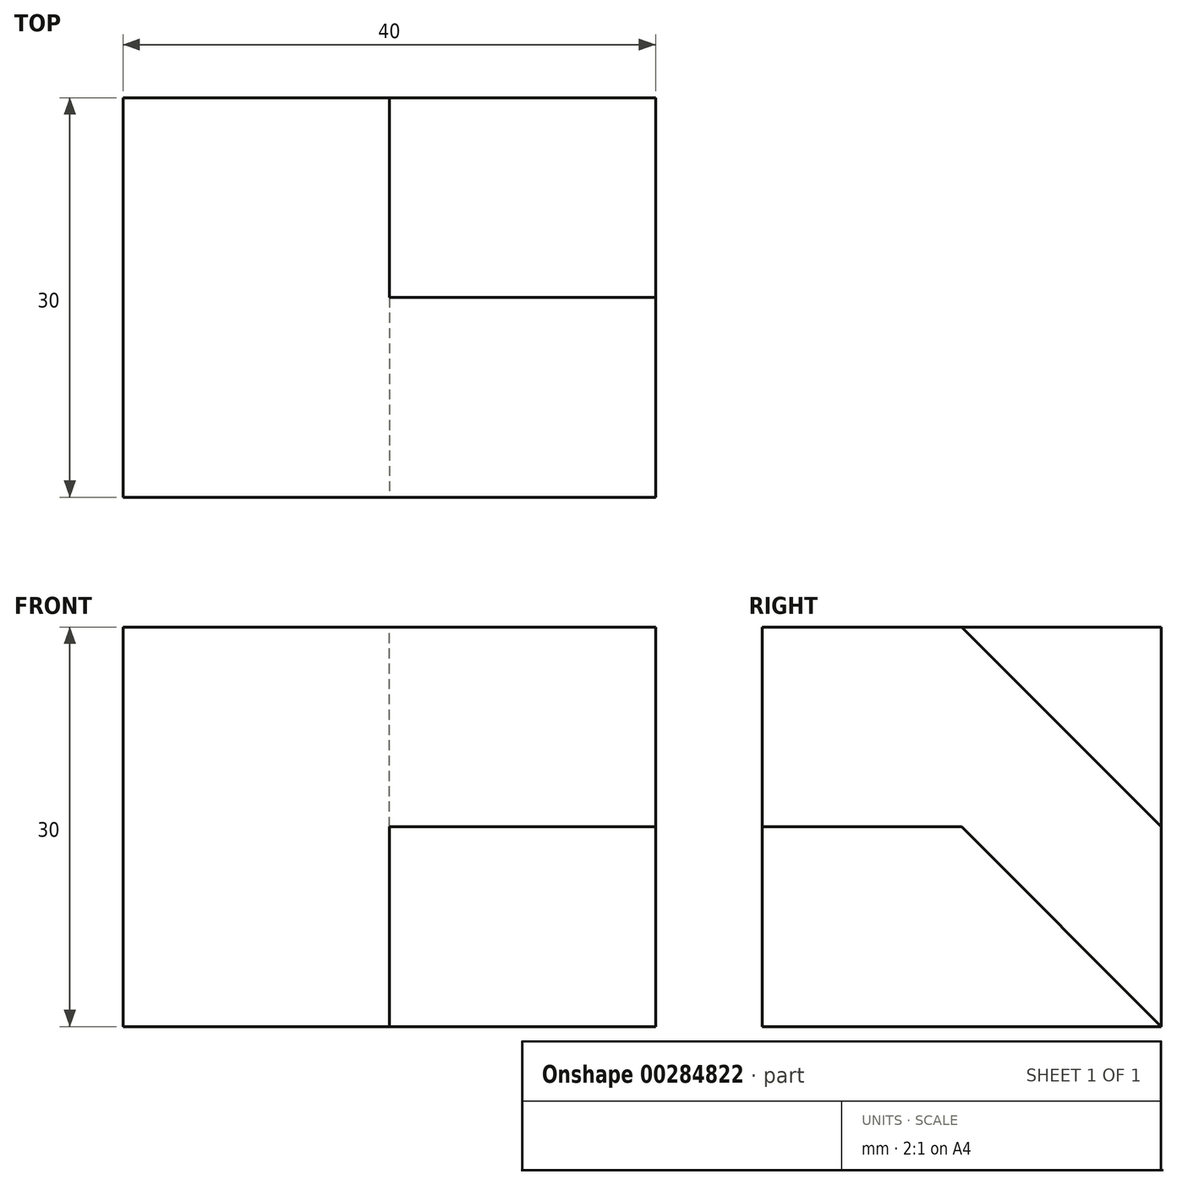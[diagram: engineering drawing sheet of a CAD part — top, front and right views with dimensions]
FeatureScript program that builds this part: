
annotation { "Feature Type Name" : "Feature", "Feature Type Description" : "" }
export const myFeature = defineFeature(function(context is Context, id is Id, definition is map)
    precondition{}
    {
        {
            var Q0;
            Q0=qCreatedBy(makeId("Right.planeOp"),FACE);
            var sketch = newSketch(context, id + "F0", { "sketchPlane" : qUnion([Q0])});
            skLineSegment(sketch, "E0.bottom", {"start": v(0, 0) * mm, "end": v(30, 0) * mm});
            skLineSegment(sketch, "E0.top", {"start": v(0, 30) * mm, "end": v(30, 30) * mm});
            skLineSegment(sketch, "E0.left", {"start": v(0, 0) * mm, "end": v(0, 30) * mm});
            skLineSegment(sketch, "E0.right", {"start": v(30, 0) * mm, "end": v(30, 30) * mm});
            skLineSegment(sketch, "E1", {"start": v(0, 15) * mm, "end": v(30, 15) * mm});
            skLineSegment(sketch, "E2", {"start": v(15, 30) * mm, "end": v(15, 0) * mm});
            skSolve(sketch);
        }
        {
            var Q0;
            Q0=qSketchRegion(id+"F0",true);
            extrude(context, id + "F1", {"entities" : qUnion([Q0]), "depth" : 20 * mm});
        }
        {
            var Q0;
            {var subQ0=sQuery(id+"F0.wireOp",EDGE,"E0.right");var subQ1=sQuery(id+"F0.wireOp",EDGE,"E0.bottom");var subQ2=makeQuery(id+"F0.imprint","INTERSECT",VERTEX,{"derivedFrom":[subQ1,subQ0]});Q0=makeQuery(id+"F0.imprint","IMPRINT",FACE,{"disambiguationData":[TD([[makeQuery(id+"F0.imprint","IMPRINT",EDGE,{"disambiguationData":[TD([[subQ2,1.0]])],"derivedFrom":subQ1}),1.0]])]});}
            var Q1;
            {var subQ0=sQuery(id+"F0.wireOp",EDGE,"E0.right");var subQ1=sQuery(id+"F0.wireOp",EDGE,"E0.top");var subQ2=makeQuery(id+"F0.imprint","INTERSECT",VERTEX,{"derivedFrom":[subQ1,subQ0]});Q1=makeQuery(id+"F0.imprint","IMPRINT",FACE,{"disambiguationData":[TD([[makeQuery(id+"F0.imprint","IMPRINT",EDGE,{"disambiguationData":[TD([[subQ2,1.0]])],"derivedFrom":subQ1}),-1.0]])]});}
            var Q2;
            {var subQ0=sQuery(id+"F0.wireOp",EDGE,"E0.left");var subQ1=sQuery(id+"F0.wireOp",EDGE,"E0.top");var subQ2=makeQuery(id+"F0.imprint","INTERSECT",VERTEX,{"derivedFrom":[subQ1,subQ0]});Q2=makeQuery(id+"F0.imprint","IMPRINT",FACE,{"disambiguationData":[TD([[makeQuery(id+"F0.imprint","IMPRINT",EDGE,{"disambiguationData":[TD([[subQ2,-1.0]])],"derivedFrom":subQ1}),-1.0]])]});}
            extrude(context, id + "F2", {"entities" : qUnion([Q0, Q1, Q2]), "operationType" : NewBodyOperationType.ADD, "depth" : 40 * mm});
        }
        {
            var Q0;
            Q0=makeQuery(id+"F2.opExtrude","CAP_FACE",FACE,{"disambiguationData":[OSD([sQuery(id+"F0.wireOp",EDGE,"E0.bottom"),sQuery(id+"F0.wireOp",EDGE,"E0.top"),sQuery(id+"F0.wireOp",EDGE,"E0.left"),sQuery(id+"F0.wireOp",EDGE,"E0.right"),sQuery(id+"F0.wireOp",EDGE,"E1"),sQuery(id+"F0.wireOp",EDGE,"E2")])],"isStart":false});
            var sketch = newSketch(context, id + "F3", { "sketchPlane" : qUnion([Q0])});
            skLineSegment(sketch, "E3", {"start": v(15, 30) * mm, "end": v(30, 15) * mm});
            skSolve(sketch);
        }
        {
            var Q0;
            {var subQ0=sQuery(id+"F3.wireOp",EDGE,"E3");Q0=makeQuery(id+"F3.imprint","IMPRINT",FACE,{"disambiguationData":[TD([[makeQuery(id+"F3.imprint","IMPRINT",EDGE,{"derivedFrom":subQ0}),1.0]])]});}
            extrude(context, id + "F4", {"entities" : qUnion([Q0]), "operationType" : NewBodyOperationType.REMOVE, "oppositeDirection" : true, "depth" : 20 * mm});
        }
        {
            var Q0;
            Q0=makeQuery(id+"F2.opExtrude","CAP_FACE",FACE,{"disambiguationData":[OSD([sQuery(id+"F0.wireOp",EDGE,"E0.bottom"),sQuery(id+"F0.wireOp",EDGE,"E0.top"),sQuery(id+"F0.wireOp",EDGE,"E0.left"),sQuery(id+"F0.wireOp",EDGE,"E0.right"),sQuery(id+"F0.wireOp",EDGE,"E1"),sQuery(id+"F0.wireOp",EDGE,"E2")])],"isStart":false});
            var sketch = newSketch(context, id + "F5", { "sketchPlane" : qUnion([Q0])});
            skLineSegment(sketch, "E4", {"start": v(15, 15) * mm, "end": v(30, 0) * mm});
            skSolve(sketch);
        }
        {
            var Q0;
            Q0=makeQuery(id+"F5.imprint","IMPRINT",FACE,{"disambiguationData":[TD([[makeQuery(id+"F5.imprint","IMPRINT",EDGE,{"derivedFrom":sQuery(id+"F5.wireOp",EDGE,"E4")}),-1.0]])]});
            extrude(context, id + "F6", {"entities" : qUnion([Q0]), "operationType" : NewBodyOperationType.REMOVE, "oppositeDirection" : true, "depth" : 20 * mm});
        }
    });
